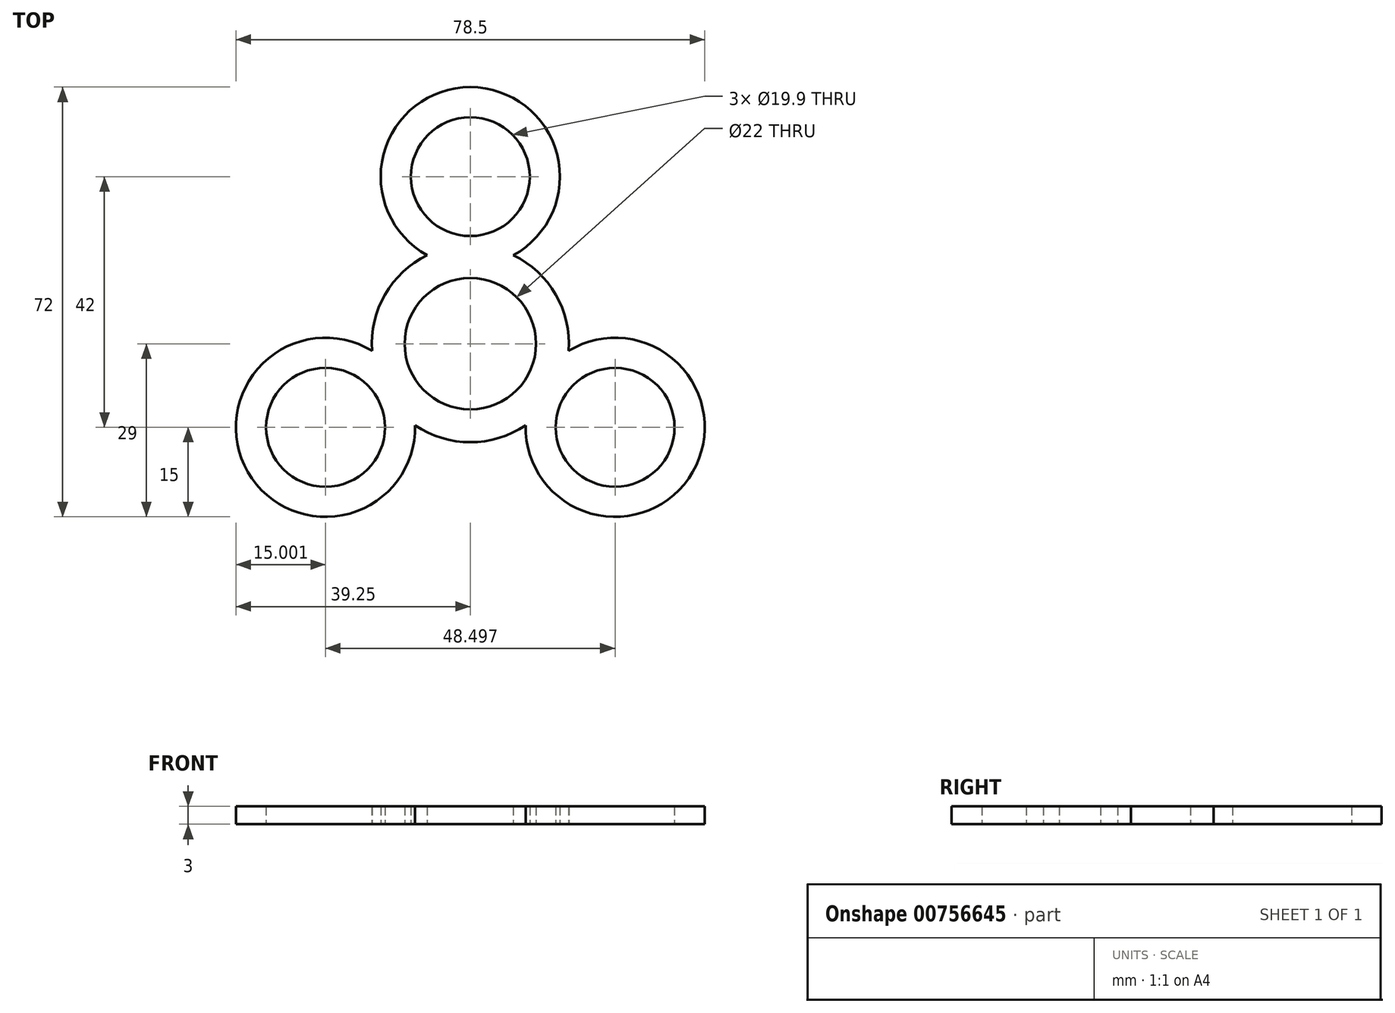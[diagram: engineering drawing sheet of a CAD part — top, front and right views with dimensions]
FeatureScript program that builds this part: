
annotation { "Feature Type Name" : "Feature", "Feature Type Description" : "" }
export const myFeature = defineFeature(function(context is Context, id is Id, definition is map)
    precondition{}
    {
        {
            var Q0;
            Q0=qCreatedBy(makeId("Top.planeOp"),FACE);
            var sketch = newSketch(context, id + "F0", { "sketchPlane" : qUnion([Q0])});
            skArc(sketch, "E0", {"start": v(9.53, 5.5) * mm, "mid": v(0, 11) * mm, "end": v(-9.53, 5.5) * mm});
            skCircle(sketch, "E1", {"center": v(0, 28) * mm, "radius": 9.95 * mm});
            skArc(sketch, "E2", {"start": v(-7.2, 14.84) * mm, "mid": v(-11.24, 12.08) * mm, "end": v(-14.29, 8.25) * mm});
            skArc(sketch, "E3", {"start": v(7.2, 14.84) * mm, "mid": v(0, 43) * mm, "end": v(-7.2, 14.84) * mm});
            skArc(sketch, "E4.trimOffspring", {"start": v(14.29, 8.25) * mm, "mid": v(11.24, 12.08) * mm, "end": v(7.2, 14.84) * mm});
            skCircle(sketch, "E5.1.0", {"center": v(-24.25, -14) * mm, "radius": 9.95 * mm});
            skArc(sketch, "E5.1.1", {"start": v(-9.25, -13.66) * mm, "mid": v(-4.84, -15.77) * mm, "end": v(0, -16.5) * mm});
            skArc(sketch, "E5.1.2", {"start": v(-9.53, 5.5) * mm, "mid": v(-9.53, -5.5) * mm, "end": v(0, -11) * mm});
            skArc(sketch, "E5.1.3", {"start": v(-14.29, 8.25) * mm, "mid": v(-16.08, 3.7) * mm, "end": v(-16.46, -1.18) * mm});
            skArc(sketch, "E5.1.4", {"start": v(-16.46, -1.18) * mm, "mid": v(-37.24, -21.5) * mm, "end": v(-9.25, -13.66) * mm});
            skCircle(sketch, "E5.2.0", {"center": v(24.25, -14) * mm, "radius": 9.95 * mm});
            skArc(sketch, "E5.2.1", {"start": v(16.46, -1.18) * mm, "mid": v(16.08, 3.7) * mm, "end": v(14.29, 8.25) * mm});
            skArc(sketch, "E5.2.2", {"start": v(0, -11) * mm, "mid": v(9.53, -5.5) * mm, "end": v(9.53, 5.5) * mm});
            skArc(sketch, "E5.2.3", {"start": v(0, -16.5) * mm, "mid": v(4.84, -15.77) * mm, "end": v(9.25, -13.66) * mm});
            skArc(sketch, "E5.2.4", {"start": v(9.25, -13.66) * mm, "mid": v(37.24, -21.5) * mm, "end": v(16.46, -1.18) * mm});
            skSolve(sketch);
        }
        {
            var Q0;
            Q0=makeQuery(id+"F0.imprint","IMPRINT",FACE,{"disambiguationData":[TD([[makeQuery(id+"F0.imprint","IMPRINT",EDGE,{"derivedFrom":sQuery(id+"F0.wireOp",EDGE,"E0")}),-1.0]])]});
            extrude(context, id + "F1", {"entities" : qUnion([Q0]), "flatOperationType" : FlatOperationType.REMOVE, "depth" : 3 * mm, "offsetDistance" : 25 * mm, "domain" : OperationDomain.MODEL});
        }
    });
